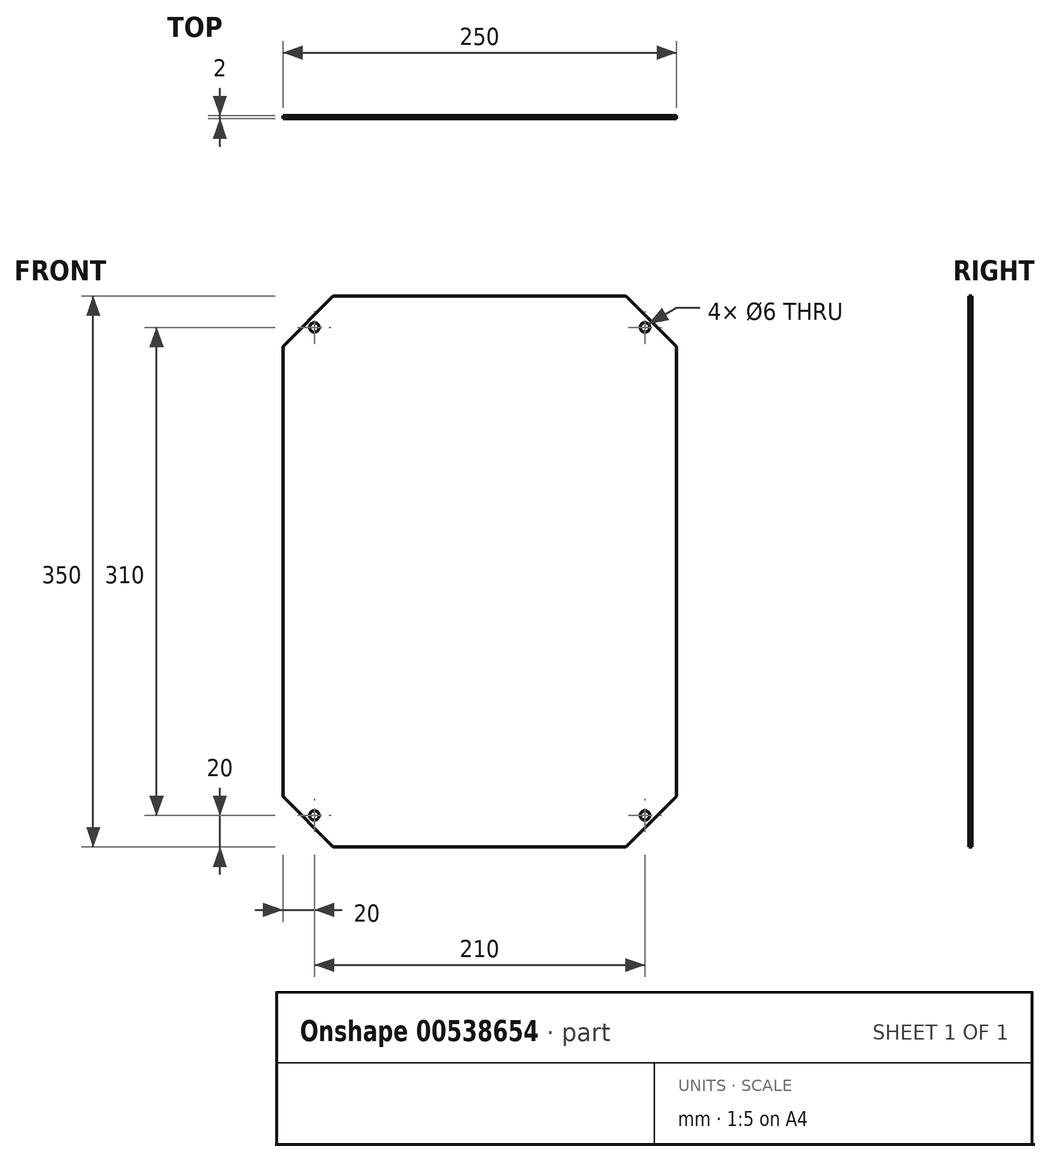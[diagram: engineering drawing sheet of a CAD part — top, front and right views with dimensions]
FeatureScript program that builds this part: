
annotation { "Feature Type Name" : "Feature", "Feature Type Description" : "" }
export const myFeature = defineFeature(function(context is Context, id is Id, definition is map)
    precondition{}
    {
        {
            var Q0;
            Q0=qCreatedBy(makeId("Front.planeOp"),FACE);
            var sketch = newSketch(context, id + "F0", { "sketchPlane" : qUnion([Q0])});
            skLineSegment(sketch, "E0.bottom", {"start": v(93, -175) * mm, "end": v(-93, -175) * mm});
            skLineSegment(sketch, "E0.top", {"start": v(93, 175) * mm, "end": v(-93, 175) * mm});
            skLineSegment(sketch, "E0.left", {"start": v(125, -143) * mm, "end": v(125, 143) * mm});
            skLineSegment(sketch, "E0.right", {"start": v(-125, -143) * mm, "end": v(-125, 143) * mm});
            skPoint(sketch, "E0.middle", {"position": v(0, 0) * mm});
            skLineSegment(sketch, "E1", {"start": v(-93, 175) * mm, "end": v(-125, 143) * mm});
            skPoint(sketch, "E2.orphan", {"position": v(-125, 175) * mm});
            skLineSegment(sketch, "E3", {"start": v(93, 175) * mm, "end": v(125, 143) * mm});
            skPoint(sketch, "E4.orphan", {"position": v(125, 175) * mm});
            skLineSegment(sketch, "E5", {"start": v(125, -143) * mm, "end": v(93, -175) * mm});
            skPoint(sketch, "E6.orphan", {"position": v(125, -175) * mm});
            skLineSegment(sketch, "E7", {"start": v(-125, -143) * mm, "end": v(-93, -175) * mm});
            skPoint(sketch, "E8.orphan", {"position": v(-125, -175) * mm});
            skLineSegment(sketch, "E9.bottom", {"start": v(-105, 155) * mm, "end": v(105, 155) * mm, "construction": true});
            skLineSegment(sketch, "E9.top", {"start": v(-105, -155) * mm, "end": v(105, -155) * mm, "construction": true});
            skLineSegment(sketch, "E9.left", {"start": v(-105, 155) * mm, "end": v(-105, -155) * mm, "construction": true});
            skLineSegment(sketch, "E9.right", {"start": v(105, 155) * mm, "end": v(105, -155) * mm, "construction": true});
            skCircle(sketch, "E10", {"center": v(-105, 155) * mm, "radius": 3 * mm});
            skCircle(sketch, "E11", {"center": v(105, 155) * mm, "radius": 3 * mm});
            skCircle(sketch, "E12", {"center": v(105, -155) * mm, "radius": 3 * mm});
            skCircle(sketch, "E13", {"center": v(-105, -155) * mm, "radius": 3 * mm});
            skSolve(sketch);
        }
        {
            var Q0;
            Q0 = qSketchRegion(id + "F0", true);
            extrude(context, id + "F1", {"entities" : qUnion([Q0]), "depth" : 2 * mm, "offsetDistance" : 25 * mm});
        }
    });
